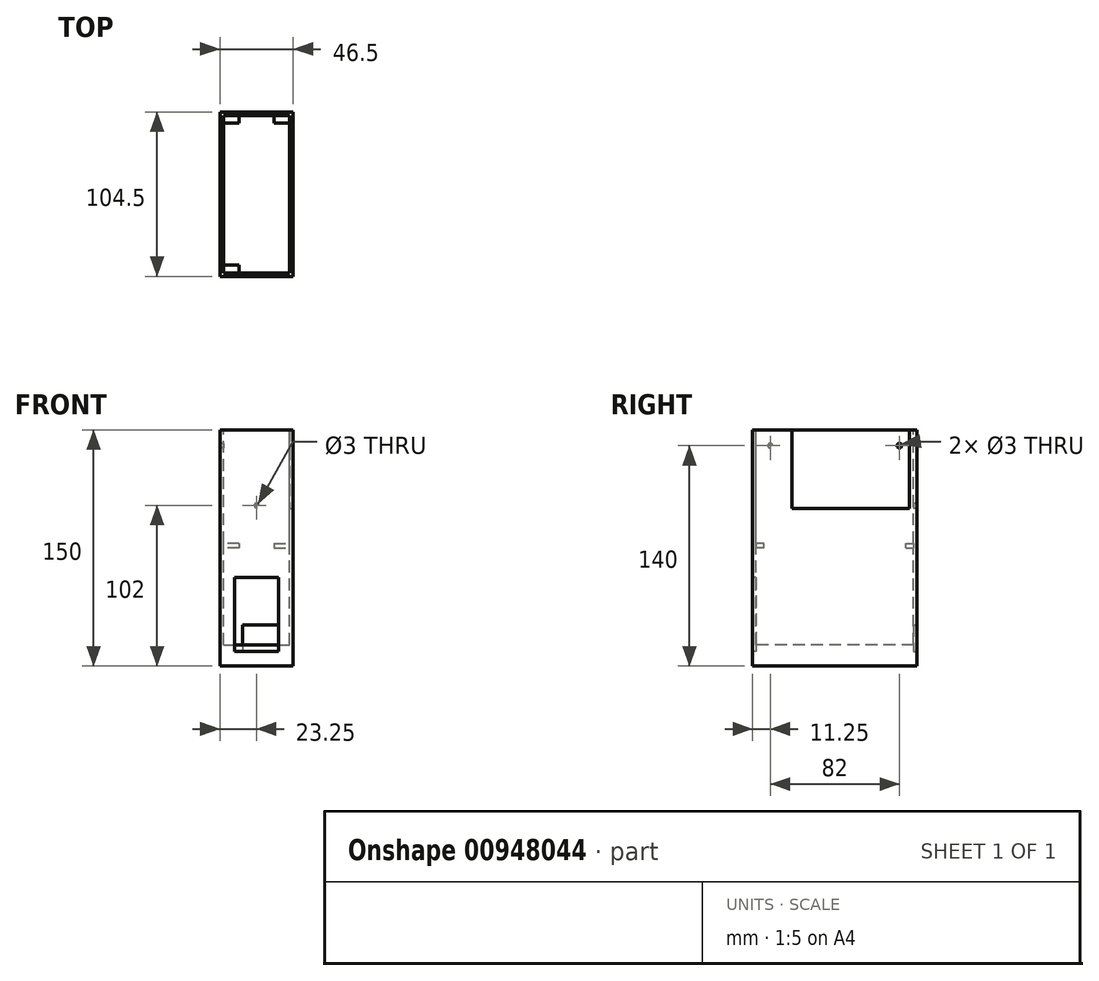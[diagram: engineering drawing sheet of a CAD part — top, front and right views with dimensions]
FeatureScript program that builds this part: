
annotation { "Feature Type Name" : "Feature", "Feature Type Description" : "" }
export const myFeature = defineFeature(function(context is Context, id is Id, definition is map)
    precondition{}
    {
        {
            var Q0;
            Q0=qCreatedBy(makeId("Front.planeOp"),FACE);
            var sketch = newSketch(context, id + "F0", { "sketchPlane" : qUnion([Q0])});
            skLineSegment(sketch, "E0.bottom", {"start": v(0, 0) * mm, "end": v(-46.5, 0) * mm});
            skLineSegment(sketch, "E0.top", {"start": v(0, -150) * mm, "end": v(-46.5, -150) * mm});
            skLineSegment(sketch, "E0.left", {"start": v(0, 0) * mm, "end": v(0, -150) * mm});
            skLineSegment(sketch, "E0.right", {"start": v(-46.5, 0) * mm, "end": v(-46.5, -150) * mm});
            skSolve(sketch);
        }
        {
            var Q0;
            Q0=makeQuery(id+"F0.imprint","IMPRINT",FACE,{"disambiguationData":[TD([[makeQuery(id+"F0.imprint","IMPRINT",EDGE,{"derivedFrom":sQuery(id+"F0.wireOp",EDGE,"E0.bottom")}),1.0]])]});
            extrude(context, id + "F1", {"entities" : qUnion([Q0]), "depth" : 104.5 * mm, "offsetDistance" : 25 * mm});
        }
        {
            var Q0;
            Q0=makeQuery(id+"F1.opExtrude","SWEPT_FACE",FACE,{"disambiguationData":[OSD([sQuery(id+"F0.wireOp",EDGE,"E0.bottom")])]});
            var sketch = newSketch(context, id + "F2", { "sketchPlane" : qUnion([Q0])});
            skLineSegment(sketch, "E1.bottom", {"start": v(-44.25, -2.25) * mm, "end": v(-2.25, -2.25) * mm});
            skLineSegment(sketch, "E1.top", {"start": v(-44.25, -102.25) * mm, "end": v(-2.25, -102.25) * mm});
            skLineSegment(sketch, "E1.left", {"start": v(-44.25, -2.25) * mm, "end": v(-44.25, -102.25) * mm});
            skLineSegment(sketch, "E1.right", {"start": v(-2.25, -2.25) * mm, "end": v(-2.25, -102.25) * mm});
            skSolve(sketch);
        }
        {
            var Q0;
            Q0=qSketchRegion(id+"F2",true);
            extrude(context, id + "F3", {"entities" : qUnion([Q0]), "operationType" : NewBodyOperationType.REMOVE, "endBound" : BoundingType.UP_TO_NEXT, "oppositeDirection" : true, "depth" : 25 * mm, "hasOffset" : true, "offsetDistance" : 2.25 * mm});
        }
        {
            var Q0;
            Q0=makeQuery(id+"F1.opExtrude","SWEPT_FACE",FACE,{"disambiguationData":[OSD([sQuery(id+"F0.wireOp",EDGE,"E0.left")])]});
            var sketch = newSketch(context, id + "F4", { "sketchPlane" : qUnion([Q0])});
            skLineSegment(sketch, "E2.bottom", {"start": v(-79.5, 0) * mm, "end": v(-5, 0) * mm});
            skLineSegment(sketch, "E2.top", {"start": v(-79.5, -50) * mm, "end": v(-5, -50) * mm});
            skLineSegment(sketch, "E2.left", {"start": v(-79.5, 0) * mm, "end": v(-79.5, -50) * mm});
            skLineSegment(sketch, "E2.right", {"start": v(-5, 0) * mm, "end": v(-5, -50) * mm});
            skSolve(sketch);
        }
        {
            var Q0;
            Q0=qSketchRegion(id+"F4",true);
            extrude(context, id + "F5", {"entities" : qUnion([Q0]), "operationType" : NewBodyOperationType.REMOVE, "oppositeDirection" : true, "depth" : 2.25 * mm, "offsetDistance" : 25 * mm});
        }
        {
            var Q0;
            Q0=makeQuery(id+"F1.opExtrude","SWEPT_FACE",FACE,{"disambiguationData":[OSD([sQuery(id+"F0.wireOp",EDGE,"E0.right")])]});
            var sketch = newSketch(context, id + "F6", { "sketchPlane" : qUnion([Q0])});
            skCircle(sketch, "E3", {"center": v(11.25, -10) * mm, "radius": 1.5 * mm});
            skCircle(sketch, "E4", {"center": v(93.25, -10) * mm, "radius": 1.5 * mm});
            skSolve(sketch);
        }
        {
            var Q0;
            Q0 = qSketchRegion(id + "F6", true);
            extrude(context, id + "F7", {"entities" : qUnion([Q0]), "operationType" : NewBodyOperationType.REMOVE, "oppositeDirection" : true, "depth" : 2.25 * mm, "offsetDistance" : 25 * mm});
        }
        {
            var Q0;
            Q0=makeQuery(id+"F1.opExtrude","CAP_FACE",FACE,{"disambiguationData":[OSD([sQuery(id+"F0.wireOp",EDGE,"E0.bottom"),sQuery(id+"F0.wireOp",EDGE,"E0.top"),sQuery(id+"F0.wireOp",EDGE,"E0.left"),sQuery(id+"F0.wireOp",EDGE,"E0.right")])],"isStart":true});
            var sketch = newSketch(context, id + "F8", { "sketchPlane" : qUnion([Q0])});
            skCircle(sketch, "E5", {"center": v(23.25, -48) * mm, "radius": 1.5 * mm});
            skSolve(sketch);
        }
        {
            var Q0;
            Q0 = qSketchRegion(id + "F8", true);
            extrude(context, id + "F9", {"entities" : qUnion([Q0]), "operationType" : NewBodyOperationType.REMOVE, "oppositeDirection" : true, "depth" : 2.25 * mm, "offsetDistance" : 25 * mm});
        }
        {
            var Q0;
            Q0=makeQuery(id+"F3.boolean.opBoolean","COPY",FACE,{"derivedFrom":makeQuery(id+"F3.opExtrude","SWEPT_FACE",FACE,{"disambiguationData":[OSD([sQuery(id+"F2.wireOp",EDGE,"E1.bottom")])]})});
            var sketch = newSketch(context, id + "F10", { "sketchPlane" : qUnion([Q0])});
            skLineSegment(sketch, "E6.bottom", {"start": v(-44.25, -72) * mm, "end": v(-34.25, -72) * mm});
            skLineSegment(sketch, "E6.top", {"start": v(-44.25, -75) * mm, "end": v(-34.25, -75) * mm});
            skLineSegment(sketch, "E6.left", {"start": v(-44.25, -72) * mm, "end": v(-44.25, -75) * mm});
            skLineSegment(sketch, "E6.right", {"start": v(-34.25, -72) * mm, "end": v(-34.25, -75) * mm});
            skLineSegment(sketch, "E7.bottom", {"start": v(-12.25, -72) * mm, "end": v(-2.25, -72) * mm});
            skLineSegment(sketch, "E7.top", {"start": v(-12.25, -75) * mm, "end": v(-2.25, -75) * mm});
            skLineSegment(sketch, "E7.left", {"start": v(-12.25, -72) * mm, "end": v(-12.25, -75) * mm});
            skLineSegment(sketch, "E7.right", {"start": v(-2.25, -72) * mm, "end": v(-2.25, -75) * mm});
            skSolve(sketch);
        }
        {
            var Q0;
            Q0 = qSketchRegion(id + "F10", true);
            extrude(context, id + "F11", {"entities" : qUnion([Q0]), "operationType" : NewBodyOperationType.ADD, "depth" : 5 * mm, "offsetDistance" : 25 * mm});
        }
        {
            var Q0;
            Q0=makeQuery(id+"F3.boolean.opBoolean","COPY",FACE,{"derivedFrom":makeQuery(id+"F3.opExtrude","SWEPT_FACE",FACE,{"disambiguationData":[OSD([sQuery(id+"F2.wireOp",EDGE,"E1.top")])]})});
            var sketch = newSketch(context, id + "F12", { "sketchPlane" : qUnion([Q0])});
            skLineSegment(sketch, "E8.bottom", {"start": v(34.25, -72) * mm, "end": v(44.25, -72) * mm});
            skLineSegment(sketch, "E8.top", {"start": v(34.25, -75) * mm, "end": v(44.25, -75) * mm});
            skLineSegment(sketch, "E8.left", {"start": v(34.25, -72) * mm, "end": v(34.25, -75) * mm});
            skLineSegment(sketch, "E8.right", {"start": v(44.25, -72) * mm, "end": v(44.25, -75) * mm});
            skSolve(sketch);
        }
        {
            var Q0;
            Q0 = qSketchRegion(id + "F12", true);
            extrude(context, id + "F13", {"entities" : qUnion([Q0]), "operationType" : NewBodyOperationType.ADD, "depth" : 5 * mm, "offsetDistance" : 25 * mm});
        }
        {
            var Q0;
            Q0=makeQuery(id+"F1.opExtrude","CAP_FACE",FACE,{"disambiguationData":[OSD([sQuery(id+"F0.wireOp",EDGE,"E0.bottom"),sQuery(id+"F0.wireOp",EDGE,"E0.top"),sQuery(id+"F0.wireOp",EDGE,"E0.left"),sQuery(id+"F0.wireOp",EDGE,"E0.right")])],"isStart":false});
            var sketch = newSketch(context, id + "F14", { "sketchPlane" : qUnion([Q0])});
            skLineSegment(sketch, "E9.bottom", {"start": v(-37.25, -93.75) * mm, "end": v(-9.25, -93.75) * mm});
            skLineSegment(sketch, "E9.top", {"start": v(-37.25, -140.75) * mm, "end": v(-9.25, -140.75) * mm});
            skLineSegment(sketch, "E9.left", {"start": v(-37.25, -93.75) * mm, "end": v(-37.25, -140.75) * mm});
            skLineSegment(sketch, "E9.right", {"start": v(-9.25, -93.75) * mm, "end": v(-9.25, -140.75) * mm});
            skSolve(sketch);
        }
        {
            var Q0;
            Q0=makeQuery(id+"F14.imprint","IMPRINT",FACE,{"disambiguationData":[TD([[makeQuery(id+"F14.imprint","IMPRINT",EDGE,{"derivedFrom":sQuery(id+"F14.wireOp",EDGE,"E9.bottom")}),-1.0]])]});
            extrude(context, id + "F15", {"entities" : qUnion([Q0]), "operationType" : NewBodyOperationType.REMOVE, "oppositeDirection" : true, "depth" : 2.25 * mm, "offsetDistance" : 25 * mm});
        }
        {
            var Q0;
            Q0=makeQuery(id+"F1.opExtrude","CAP_FACE",FACE,{"disambiguationData":[OSD([sQuery(id+"F0.wireOp",EDGE,"E0.bottom"),sQuery(id+"F0.wireOp",EDGE,"E0.top"),sQuery(id+"F0.wireOp",EDGE,"E0.left"),sQuery(id+"F0.wireOp",EDGE,"E0.right")])],"isStart":true});
            var sketch = newSketch(context, id + "F16", { "sketchPlane" : qUnion([Q0])});
            skLineSegment(sketch, "E10.bottom", {"start": v(9.25, -123.75) * mm, "end": v(32.25, -123.75) * mm});
            skLineSegment(sketch, "E10.top", {"start": v(9.25, -140.75) * mm, "end": v(32.25, -140.75) * mm});
            skLineSegment(sketch, "E10.left", {"start": v(9.25, -123.75) * mm, "end": v(9.25, -140.75) * mm});
            skLineSegment(sketch, "E10.right", {"start": v(32.25, -123.75) * mm, "end": v(32.25, -140.75) * mm});
            skSolve(sketch);
        }
        {
            var Q0;
            Q0 = qSketchRegion(id + "F16", true);
            extrude(context, id + "F17", {"entities" : qUnion([Q0]), "operationType" : NewBodyOperationType.REMOVE, "oppositeDirection" : true, "depth" : 2.25 * mm, "offsetDistance" : 25 * mm});
        }
    });
